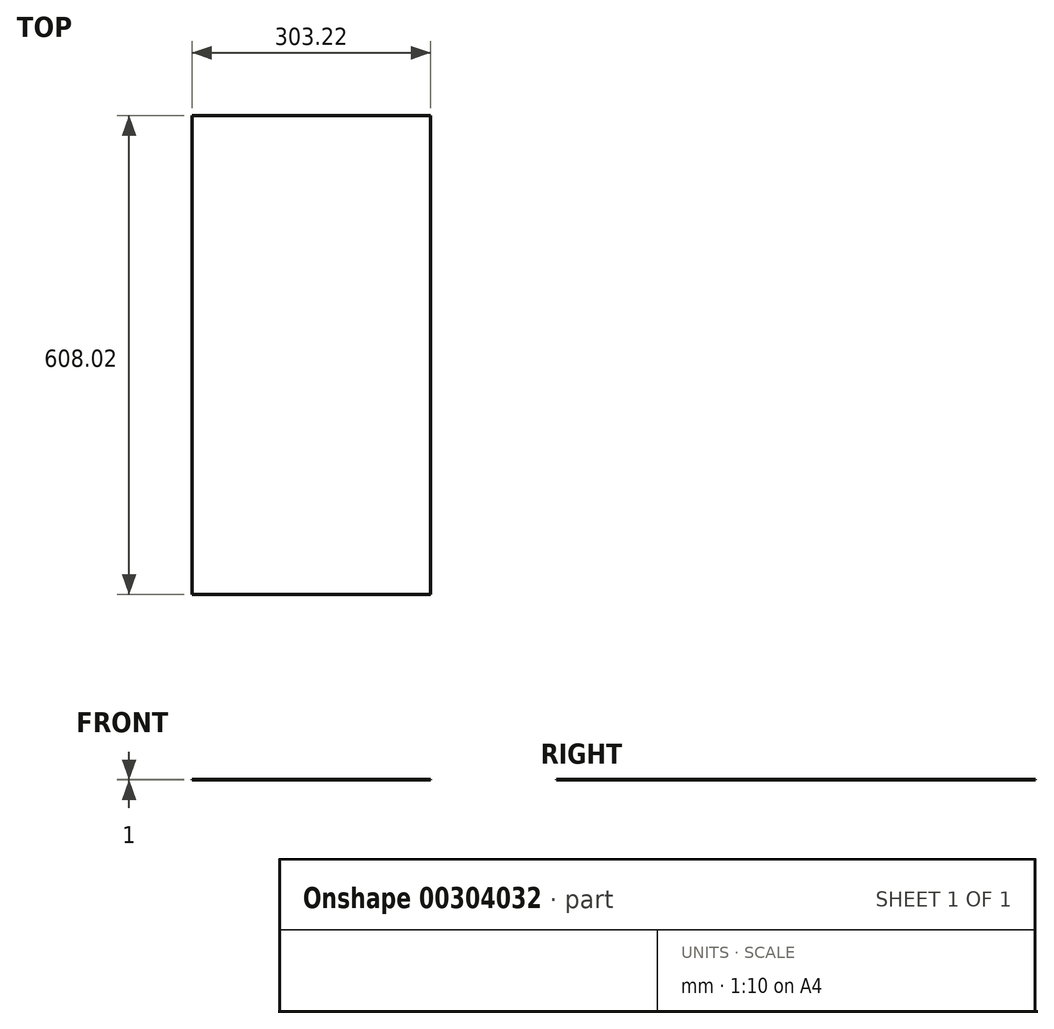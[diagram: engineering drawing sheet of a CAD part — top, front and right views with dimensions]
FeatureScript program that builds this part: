
annotation { "Feature Type Name" : "Feature", "Feature Type Description" : "" }
export const myFeature = defineFeature(function(context is Context, id is Id, definition is map)
    precondition{}
    {
        {
            var Q0;
            Q0=qCreatedBy(makeId("Top.planeOp"),FACE);
            var sketch = newSketch(context, id + "F0", { "sketchPlane" : qUnion([Q0])});
            skLineSegment(sketch, "E0.bottom", {"start": v(151.6, 304) * mm, "end": v(-151.6, 304) * mm});
            skLineSegment(sketch, "E0.top", {"start": v(151.6, -304) * mm, "end": v(-151.6, -304) * mm});
            skLineSegment(sketch, "E0.left", {"start": v(151.6, 304) * mm, "end": v(151.6, -304) * mm});
            skLineSegment(sketch, "E0.right", {"start": v(-151.6, 304) * mm, "end": v(-151.6, -304) * mm});
            skPoint(sketch, "E0.middle", {"position": v(0, 0) * mm});
            skSolve(sketch);
        }
        {
            var Q0;
            Q0 = qSketchRegion(id + "F0", true);
            extrude(context, id + "F1", {"entities" : qUnion([Q0]), "depth" : 1 * mm});
        }
    });
